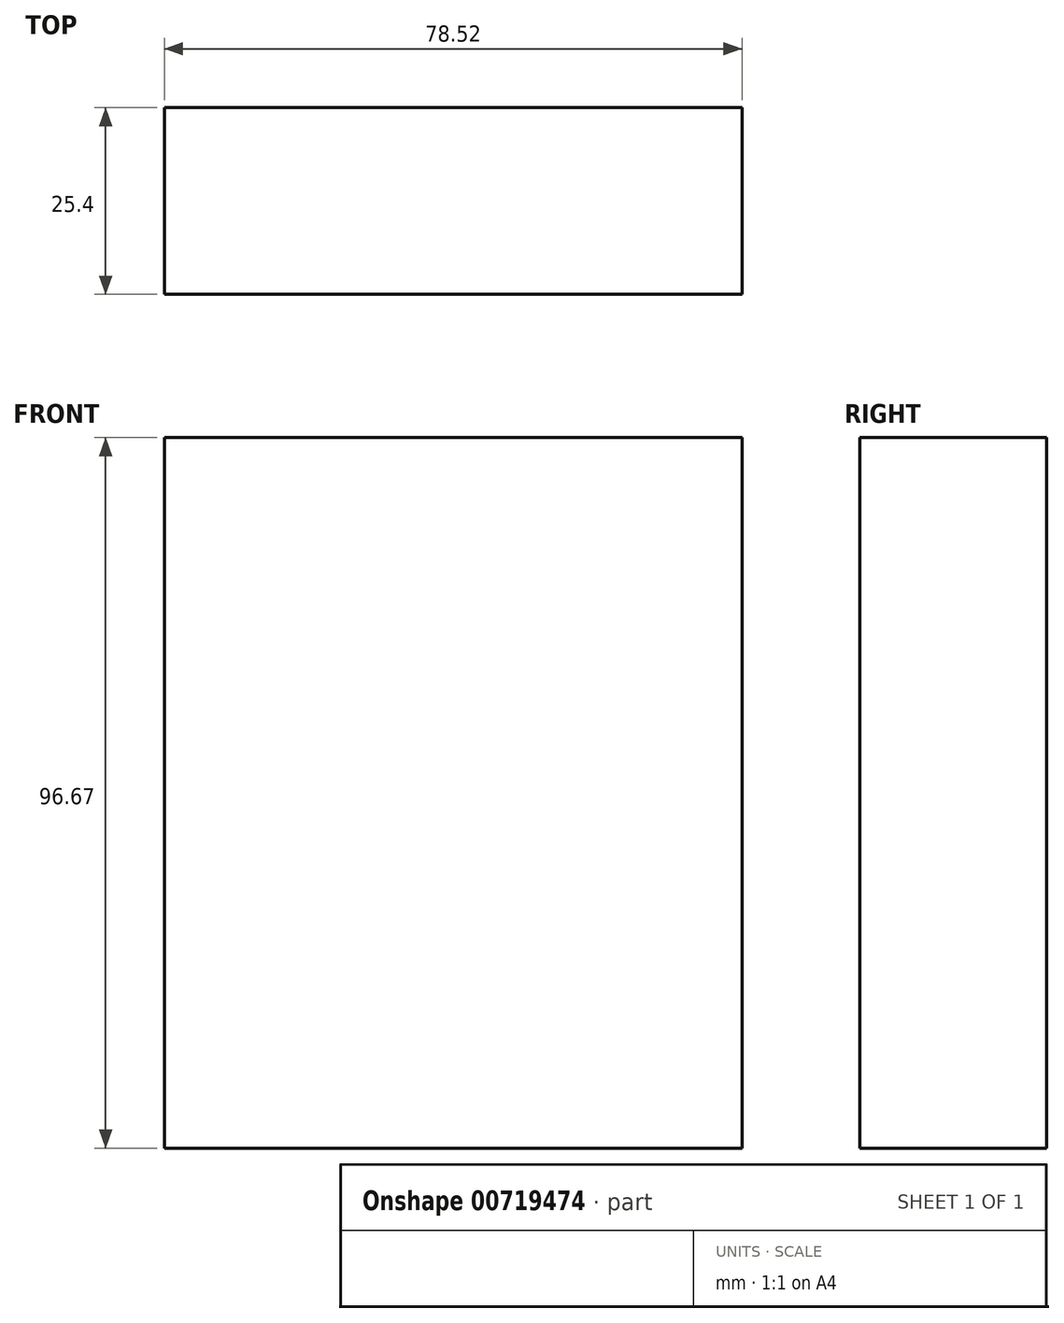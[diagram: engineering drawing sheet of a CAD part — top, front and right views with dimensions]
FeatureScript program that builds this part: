
annotation { "Feature Type Name" : "Feature", "Feature Type Description" : "" }
export const myFeature = defineFeature(function(context is Context, id is Id, definition is map)
    precondition{}
    {
        {
            var Q0;
            Q0=qCreatedBy(makeId("Front.planeOp"),FACE);
            var sketch = newSketch(context, id + "F0", { "sketchPlane" : qUnion([Q0])});
            skLineSegment(sketch, "E0.bottom", {"start": v(-10.1, 0) * mm, "end": v(-88.62, 0) * mm});
            skLineSegment(sketch, "E0.top", {"start": v(-10.1, 96.67) * mm, "end": v(-88.62, 96.67) * mm});
            skLineSegment(sketch, "E0.left", {"start": v(-10.1, 0) * mm, "end": v(-10.1, 96.67) * mm});
            skLineSegment(sketch, "E0.right", {"start": v(-88.62, 0) * mm, "end": v(-88.62, 96.67) * mm});
            skPoint(sketch, "E0.middle", {"position": v(-49.36, 48.34) * mm});
            skSolve(sketch);
        }
        {
            var Q0;
            Q0 = qSketchRegion(id + "F0", true);
            extrude(context, id + "F1", {"entities" : qUnion([Q0]), "depth" : 25.4 * mm, "offsetDistance" : 25.4 * mm});
        }
    });
